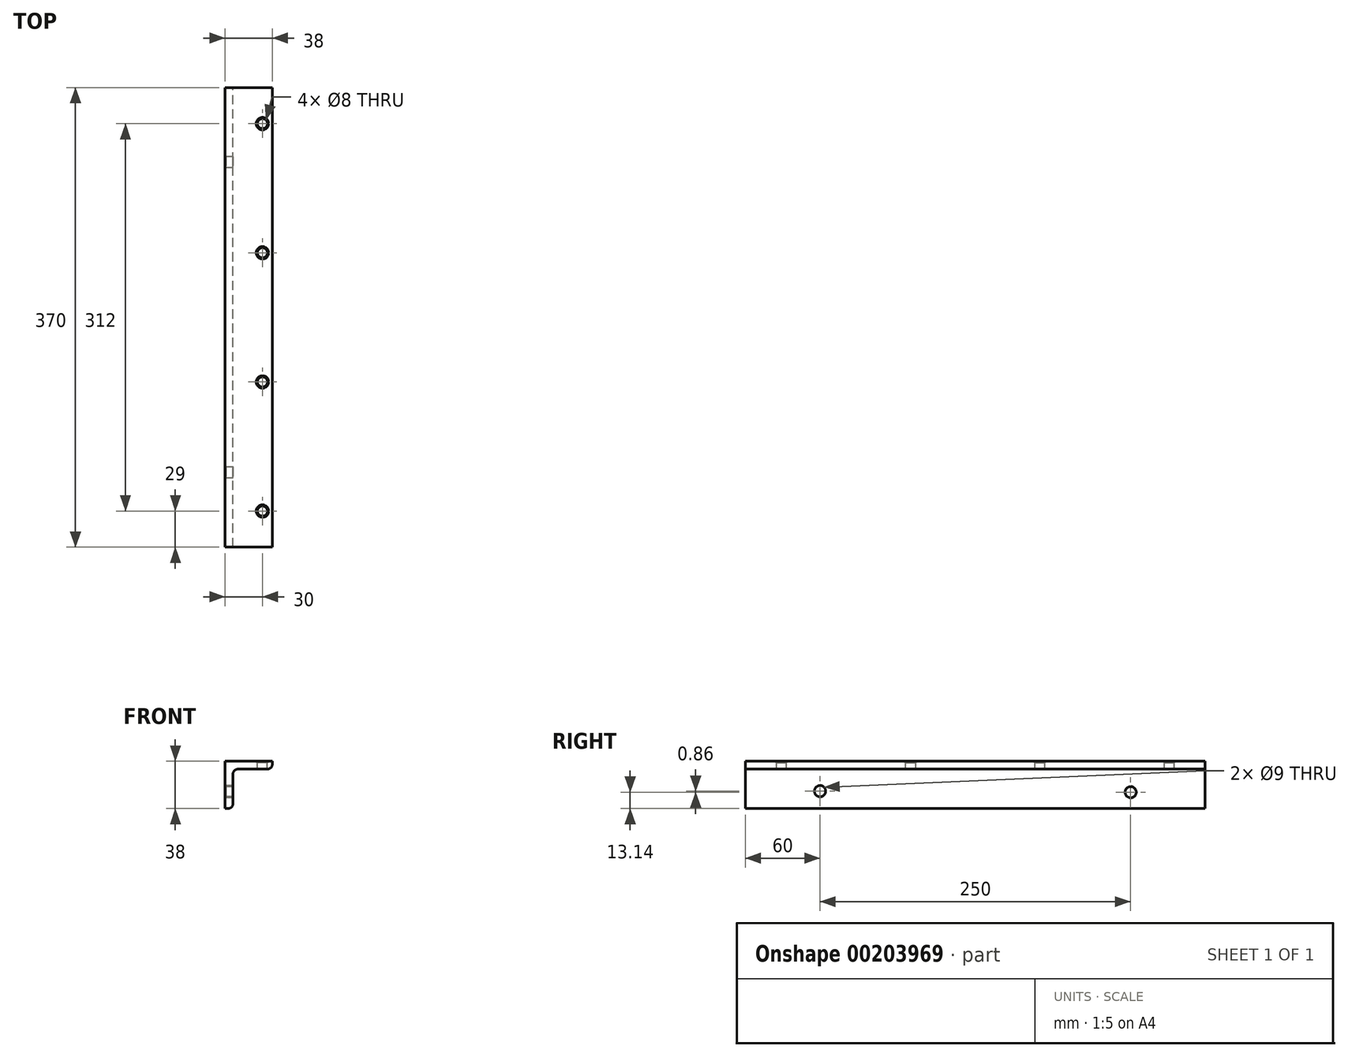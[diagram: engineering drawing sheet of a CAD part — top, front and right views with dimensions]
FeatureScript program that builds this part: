
annotation { "Feature Type Name" : "Feature", "Feature Type Description" : "" }
export const myFeature = defineFeature(function(context is Context, id is Id, definition is map)
    precondition{}
    {
        {
            var Q0;
            Q0=qCreatedBy(makeId("Front.planeOp"),FACE);
            var sketch = newSketch(context, id + "F0", { "sketchPlane" : qUnion([Q0])});
            skLineSegment(sketch, "E0", {"start": v(0, 0) * mm, "end": v(0, -38) * mm});
            skLineSegment(sketch, "E1", {"start": v(0, 0) * mm, "end": v(38, 0) * mm});
            skLineSegment(sketch, "E2", {"start": v(0, -38) * mm, "end": v(6.3, -38) * mm});
            skLineSegment(sketch, "E3", {"start": v(6.3, -38) * mm, "end": v(6.3, -6.3) * mm});
            skPoint(sketch, "E4.end.orphan", {"position": v(38.47, -6.3) * mm});
            skLineSegment(sketch, "E5", {"start": v(38, 0) * mm, "end": v(38, -6.3) * mm});
            skLineSegment(sketch, "E6", {"start": v(38, -6.3) * mm, "end": v(6.3, -6.3) * mm});
            skSolve(sketch);
        }
        {
            var Q0;
            Q0=makeQuery(id+"F0.imprint","IMPRINT",FACE,{"disambiguationData":[TD([[makeQuery(id+"F0.imprint","IMPRINT",EDGE,{"derivedFrom":sQuery(id+"F0.wireOp",EDGE,"E0")}),1.0]])]});
            extrude(context, id + "F1", {"entities" : qUnion([Q0]), "depth" : 370 * mm});
        }
        {
            var Q0;
            Q0=makeQuery(id+"F1.opExtrude","SWEPT_EDGE",EDGE,{"disambiguationData":[OSD([sQuery(id+"F0.wireOp",EDGE,"E2"),sQuery(id+"F0.wireOp",EDGE,"E3")])]});
            var Q1;
            Q1=makeQuery(id+"F1.opExtrude","SWEPT_EDGE",EDGE,{"disambiguationData":[OSD([sQuery(id+"F0.wireOp",EDGE,"E5"),sQuery(id+"F0.wireOp",EDGE,"E6")])]});
            fillet(context, id + "F2", {"entities" : qUnion([Q0, Q1]), "radius" : 4 * mm, "tangentPropagation" : true, "allowEdgeOverflow" : false});
        }
        {
            var Q0;
            Q0=makeQuery(id+"F1.opExtrude","SWEPT_EDGE",EDGE,{"disambiguationData":[OSD([sQuery(id+"F0.wireOp",EDGE,"E3"),sQuery(id+"F0.wireOp",EDGE,"E6")])]});
            fillet(context, id + "F3", {"entities" : qUnion([Q0]), "radius" : 4 * mm, "tangentPropagation" : true, "allowEdgeOverflow" : false});
        }
        {
            var Q0;
            Q0=makeQuery(id+"F1.opExtrude","SWEPT_FACE",FACE,{"disambiguationData":[OSD([sQuery(id+"F0.wireOp",EDGE,"E1")])]});
            var sketch = newSketch(context, id + "F4", { "sketchPlane" : qUnion([Q0])});
            skPoint(sketch, "E7", {"position": v(30.84, -897.16) * mm});
            skPoint(sketch, "E8", {"position": v(30.84, 520.75) * mm});
            skPoint(sketch, "E9", {"position": v(30.84, -577.84) * mm});
            skPoint(sketch, "E10", {"position": v(30.84, 152.02) * mm});
            skPoint(sketch, "E11", {"position": v(30, -341) * mm});
            skPoint(sketch, "E12", {"position": v(30, -237) * mm});
            skPoint(sketch, "E13", {"position": v(30, -133) * mm});
            skPoint(sketch, "E14", {"position": v(30, -29) * mm});
            skSolve(sketch);
        }
        {
            var Q0;
            Q0=sQuery(id+"F4.wireOp",VERTEX,"E11");
            var Q1;
            Q1=sQuery(id+"F4.wireOp",VERTEX,"E12");
            var Q2;
            Q2=sQuery(id+"F4.wireOp",VERTEX,"E13");
            var Q3;
            Q3=sQuery(id+"F4.wireOp",VERTEX,"E14");
            var Q4;
            Q4=makeQuery(id+"F1.opExtrude","SWEPT_BODY",BODY,{"disambiguationData":[OSD([sQuery(id+"F0.wireOp",EDGE,"E0"),sQuery(id+"F0.wireOp",EDGE,"E1"),sQuery(id+"F0.wireOp",EDGE,"E2"),sQuery(id+"F0.wireOp",EDGE,"E3"),sQuery(id+"F0.wireOp",EDGE,"E5"),sQuery(id+"F0.wireOp",EDGE,"E6")])]});
            hole(context, id + "F5", {"style" : HoleStyle.C_SINK, "endStyle" : HoleEndStyle.THROUGH, "holeDiameter" : 8 * mm, "cSinkDiameter" : 10 * mm, "cSinkAngle" : 90 * degree, "startFromSketch" : true, "locations" : qUnion([Q0, Q1, Q2, Q3]), "scope" : qUnion([Q4]), "isTappedThrough" : true});
        }
        {
            var Q0;
            Q0=makeQuery(id+"F1.opExtrude","SWEPT_FACE",FACE,{"disambiguationData":[OSD([sQuery(id+"F0.wireOp",EDGE,"E0")])]});
            var sketch = newSketch(context, id + "F6", { "sketchPlane" : qUnion([Q0])});
            skPoint(sketch, "E15", {"position": v(310, -24) * mm});
            skPoint(sketch, "E16", {"position": v(60, -24.86) * mm});
            skSolve(sketch);
        }
        {
            var Q0;
            Q0=sQuery(id+"F6.wireOp",VERTEX,"E15");
            var Q1;
            Q1=sQuery(id+"F6.wireOp",VERTEX,"E16");
            var Q2;
            Q2=makeQuery(id+"F1.opExtrude","SWEPT_BODY",BODY,{"disambiguationData":[OSD([sQuery(id+"F0.wireOp",EDGE,"E0"),sQuery(id+"F0.wireOp",EDGE,"E1"),sQuery(id+"F0.wireOp",EDGE,"E2"),sQuery(id+"F0.wireOp",EDGE,"E3"),sQuery(id+"F0.wireOp",EDGE,"E5"),sQuery(id+"F0.wireOp",EDGE,"E6")])]});
            hole(context, id + "F7", {"style" : HoleStyle.C_SINK, "endStyle" : HoleEndStyle.THROUGH, "holeDiameter" : 9 * mm, "cSinkDiameter" : 10 * mm, "cSinkAngle" : 90 * degree, "startFromSketch" : true, "locations" : qUnion([Q0, Q1]), "scope" : qUnion([Q2]), "isTappedThrough" : true});
        }
    });
